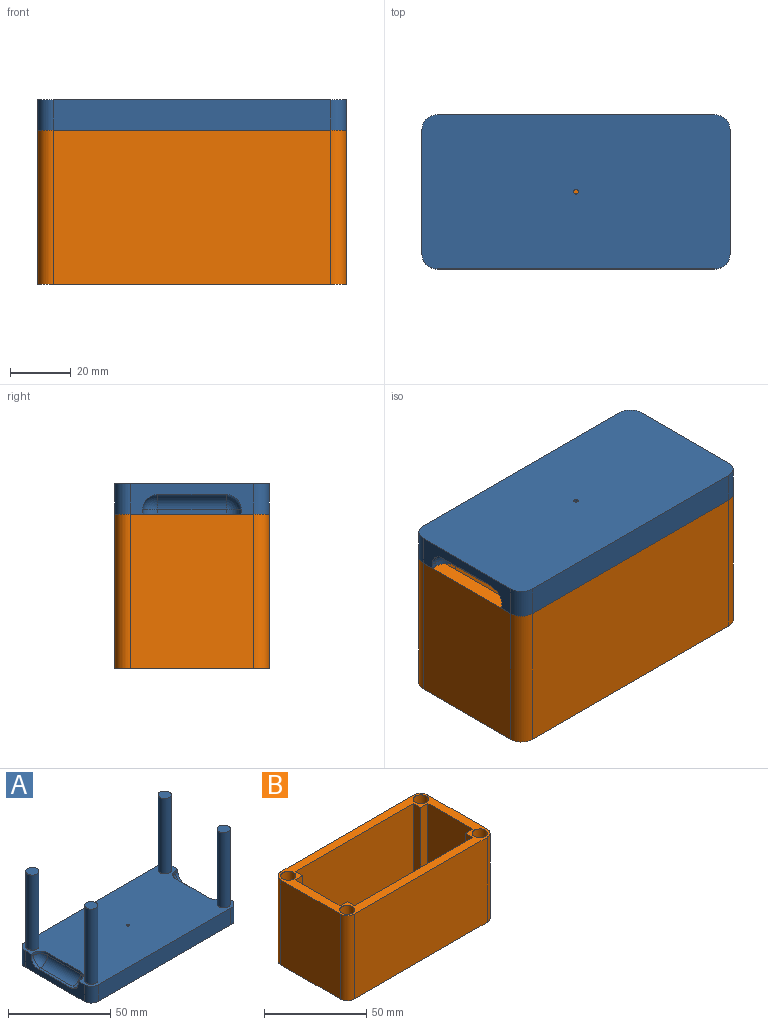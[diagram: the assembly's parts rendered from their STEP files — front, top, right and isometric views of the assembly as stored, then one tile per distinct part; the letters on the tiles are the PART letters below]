
ASSEMBLY  parts=2 mates=1
PART A: 41 faces, bbox 101.6x50.8x55 mm
  f0: plane 101.6x50.8mm, normal (0,0,1), area 4604.3mm2, adj f1,f2,f3,f4,f5,f6,f7,f8
  f1: plane 91.6x10mm, normal (0,1,0), area 916mm2, adj f0,f2,f9,f10
  f2: cylinder r=5mm len=10mm, axis (0,0,-1), area 78.5mm2, adj f0,f1,f3,f10
  f3: plane 40.8x10mm, normal (-1,0,0), area 207.5mm2, adj f0,f2,f4,f10,f30,f31,f32,f33
  f4: cylinder r=5mm len=10mm, axis (0,0,-1), area 78.5mm2, adj f0,f3,f5,f10
  f5: plane 91.6x10mm, normal (0,-1,0), area 916mm2, adj f0,f4,f6,f10
  f6: cylinder r=5mm len=10mm, axis (0,0,-1), area 78.5mm2, adj f0,f5,f7,f10
  f7: plane 40.8x10mm, normal (1,0,0), area 207.5mm2, adj f0,f6,f9,f10,f19,f20,f21,f22
  f8: cylinder r=0.75mm len=10mm, axis (0,0,-1), area 47.1mm2, adj f0,f10
  f9: cylinder r=5mm len=10mm, axis (0,0,-1), area 78.5mm2, adj f0,f1,f7,f10
  f10: plane 101.6x50.8mm, normal (0,0,-1), area 5138.1mm2, adj f1,f2,f3,f4,f5,f6,f7,f8
  f11: cylinder r=3.25mm len=45mm, axis (0,0,-1), area 918.9mm2, adj f0,f12
  f12: plane 6.5x6.5mm, normal (0,0,1), area 33.2mm2, adj f11
  f13: cylinder r=3.25mm len=45mm, axis (0,0,-1), area 918.9mm2, adj f0,f14
  f14: plane 6.5x6.5mm, normal (0,0,1), area 33.2mm2, adj f13
  f15: cylinder r=3.25mm len=45mm, axis (0,0,-1), area 918.9mm2, adj f0,f16
  f16: plane 6.5x6.5mm, normal (0,0,1), area 33.2mm2, adj f15
  f17: cylinder r=3.25mm len=45mm, axis (0,0,-1), area 918.9mm2, adj f0,f18
  f18: plane 6.5x6.5mm, normal (0,0,1), area 33.2mm2, adj f17
  f19: plane 1.5x1.5mm, normal (0,-1,0), area 2.2mm2, adj f0,f7,f23,f29
  f20: plane 1.5x1.5mm, normal (0,1,0), area 2.2mm2, adj f0,f7,f21,f25
  f21: cylinder r=5mm len=5mm, axis (1,0,0), area 11.8mm2, adj f7,f20,f22,f26
  f22: plane 22.5x1.5mm, normal (0,0,1), area 33.7mm2, adj f7,f21,f23,f27
  f23: cylinder r=5mm len=5mm, axis (1,0,0), area 11.8mm2, adj f7,f19,f22,f28
  f24: plane 22.5x1.5mm, normal (1,0,0), area 33.8mm2, adj f0,f25,f27,f29
  f25: cylinder r=5mm len=5mm, axis (0,0,-1), area 11.8mm2, adj f0,f20,f24,f26
  f26: sphere r=5mm, area 39.3mm2, adj f21,f25,f27
  f27: cylinder r=5mm len=22.5mm, axis (0,1,0), area 176.7mm2, adj f22,f24,f26,f28
  f28: sphere r=5mm, area 39.3mm2, adj f23,f27,f29
  f29: cylinder r=5mm len=5mm, axis (0,0,1), area 11.8mm2, adj f0,f19,f24,f28
  f30: plane 1.5x1.5mm, normal (0,-1,0), area 2.3mm2, adj f0,f3,f31,f40
  f31: cylinder r=5mm len=5mm, axis (-1,0,0), area 11.8mm2, adj f3,f30,f32,f39
  f32: plane 22.5x1.5mm, normal (0,0,1), area 33.8mm2, adj f3,f31,f33,f38
  f33: cylinder r=5mm len=5mm, axis (-1,0,0), area 11.8mm2, adj f3,f32,f34,f37
  f34: plane 1.5x1.5mm, normal (0,1,0), area 2.3mm2, adj f0,f3,f33,f36
  f35: plane 22.5x1.5mm, normal (-1,0,0), area 33.7mm2, adj f0,f36,f38,f40
  f36: cylinder r=5mm len=5mm, axis (0,0,1), area 11.8mm2, adj f0,f34,f35,f37
  f37: sphere r=5mm, area 39.3mm2, adj f33,f36,f38
  f38: cylinder r=5mm len=22.5mm, axis (0,-1,0), area 176.7mm2, adj f32,f35,f37,f39
  f39: sphere r=5mm, area 39.3mm2, adj f31,f38,f40
  f40: cylinder r=5mm len=5mm, axis (0,0,-1), area 11.8mm2, adj f0,f30,f35,f39
PART B: 35 faces, bbox 101.6x50.8x50.8 mm
  f0: plane 91.6x40.8mm, normal (0,0,1), area 3637.3mm2, adj f1,f2,f3,f4,f15,f16,f17,f18
  f1: plane 45.8x30.8mm, normal (1,0,0), area 1410.6mm2, adj f0,f14,f19,f21
  f2: plane 81.6x45.8mm, normal (0,1,0), area 3737.3mm2, adj f0,f14,f18,f20
  f3: plane 45.8x30.8mm, normal (-1,0,0), area 1410.6mm2, adj f0,f14,f15,f17
  f4: plane 81.6x45.8mm, normal (0,-1,0), area 3737.3mm2, adj f0,f14,f16,f22
  f5: plane 91.6x50.8mm, normal (0,1,0), area 4653.3mm2, adj f6,f12,f13,f14
  f6: cylinder r=5mm len=50.8mm, axis (0,0,-1), area 399mm2, adj f5,f7,f13,f14
  f7: plane 50.8x40.8mm, normal (-1,0,0), area 2072.6mm2, adj f6,f8,f13,f14
  f8: cylinder r=5mm len=50.8mm, axis (0,0,-1), area 399mm2, adj f7,f9,f13,f14
  f9: plane 91.6x50.8mm, normal (0,-1,0), area 4653.3mm2, adj f8,f10,f13,f14
  f10: cylinder r=5mm len=50.8mm, axis (0,0,-1), area 399mm2, adj f9,f11,f13,f14
  f11: plane 50.8x40.8mm, normal (1,0,0), area 2072.6mm2, adj f10,f12,f13,f14
  f12: cylinder r=5mm len=50.8mm, axis (0,0,-1), area 399mm2, adj f5,f11,f13,f14
  f13: plane 101.6x50.8mm, normal (0,0,-1), area 5132.8mm2, adj f5,f6,f7,f8,f9,f10,f11,f12
  f14: plane 101.6x50.8mm, normal (0,0,1), area 1325.8mm2, adj f1,f2,f3,f4,f5,f6,f7,f8
  f15: plane 45.8x5mm, normal (0,-1,0), area 229mm2, adj f0,f3,f14,f16
  f16: plane 45.8x5mm, normal (-1,0,0), area 229mm2, adj f0,f4,f14,f15
  f17: plane 45.8x5mm, normal (0,1,0), area 229mm2, adj f0,f3,f14,f18
  f18: plane 45.8x5mm, normal (-1,0,0), area 229mm2, adj f0,f2,f14,f17
  f19: plane 45.8x5mm, normal (0,1,0), area 229mm2, adj f0,f1,f14,f20
  f20: plane 45.8x5mm, normal (1,0,0), area 229mm2, adj f0,f2,f14,f19
  f21: plane 45.8x5mm, normal (0,-1,0), area 229mm2, adj f0,f1,f14,f22
  f22: plane 45.8x5mm, normal (1,0,0), area 229mm2, adj f0,f4,f14,f21
  f23: cylinder r=3.75mm len=45mm, axis (0,0,1), area 1060.3mm2, adj f14,f24
  f24: plane 7.5x7.5mm, normal (0,0,1), area 42.4mm2, adj f23,f34
  f25: cylinder r=3.75mm len=45mm, axis (0,0,1), area 1060.3mm2, adj f14,f26
  f26: plane 7.5x7.5mm, normal (0,0,1), area 42.4mm2, adj f25,f33
  f27: cylinder r=3.75mm len=45mm, axis (0,0,1), area 1060.3mm2, adj f14,f28
  f28: plane 7.5x7.5mm, normal (0,0,1), area 42.4mm2, adj f27,f32
  f29: cylinder r=3.75mm len=45mm, axis (0,0,1), area 1060.3mm2, adj f14,f30
  f30: plane 7.5x7.5mm, normal (0,0,1), area 42.4mm2, adj f29,f31
  f31: cylinder r=0.75mm len=5.8mm, axis (0,0,1), area 27.3mm2, adj f13,f30
  f32: cylinder r=0.75mm len=5.8mm, axis (0,0,1), area 27.3mm2, adj f13,f28
  f33: cylinder r=0.75mm len=5.8mm, axis (0,0,1), area 27.3mm2, adj f13,f26
  f34: cylinder r=0.75mm len=5.8mm, axis (0,0,1), area 27.3mm2, adj f13,f24
PLACE A rot(axis=(1,0,0),180deg) t=(-222.91,22.46,-563.72)mm
PLACE B t=(-234.58,-32.82,-624.52)mm
MATE slider B.f6 <-> A.f4  axis (0,0,1) through (-280.38,-12.42,-573.72)mm
